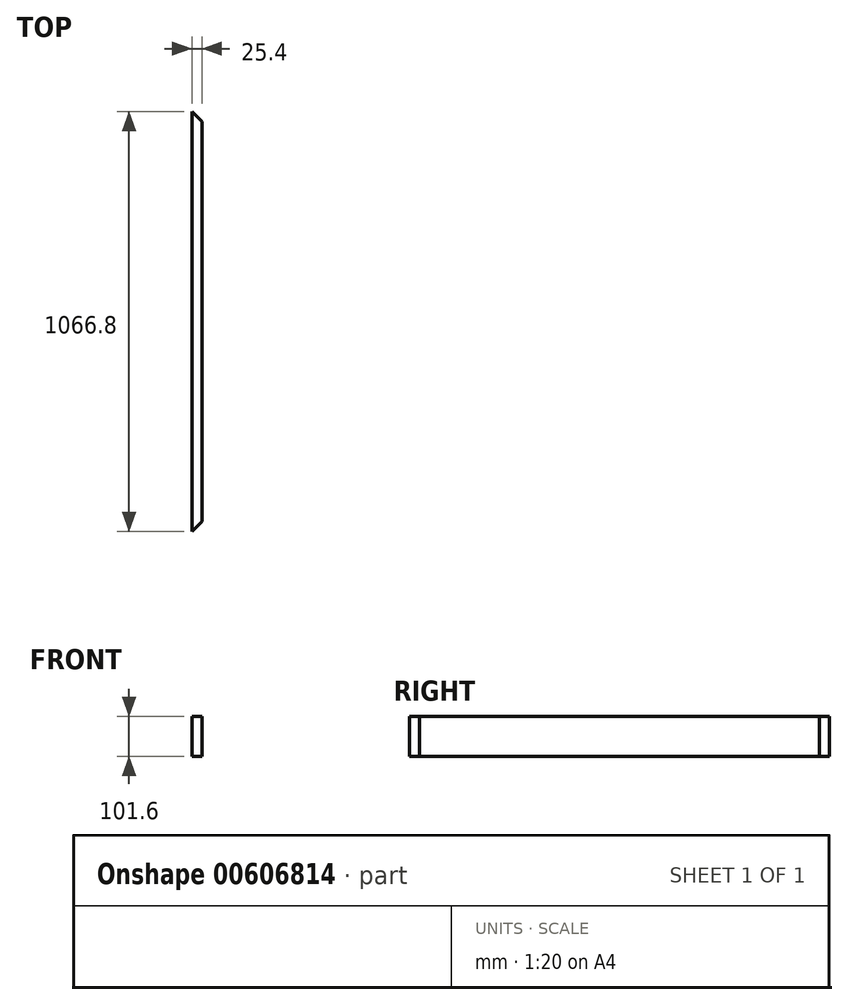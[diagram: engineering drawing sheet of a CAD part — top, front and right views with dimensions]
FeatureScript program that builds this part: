
annotation { "Feature Type Name" : "Feature", "Feature Type Description" : "" }
export const myFeature = defineFeature(function(context is Context, id is Id, definition is map)
    precondition{}
    {
        {
            var Q0;
            Q0=qCreatedBy(makeId("Top.planeOp"),FACE);
            var sketch = newSketch(context, id + "F0", { "sketchPlane" : qUnion([Q0])});
            skLineSegment(sketch, "E0", {"start": v(-11.08, 647.02) * mm, "end": v(14.32, 621.62) * mm});
            skPoint(sketch, "E1.endSnap0", {"position": v(-11.08, 75.52) * mm});
            skLineSegment(sketch, "E2.MirrorCS", {"start": v(-11.08, -546.78) * mm, "end": v(14.32, -521.38) * mm});
            skLineSegment(sketch, "E3", {"start": v(-11.08, -419.78) * mm, "end": v(14.32, -394.38) * mm});
            skLineSegment(sketch, "E4", {"start": v(14.32, 621.62) * mm, "end": v(14.32, -394.38) * mm});
            skLineSegment(sketch, "E5", {"start": v(-11.08, 647.02) * mm, "end": v(-11.08, -419.78) * mm});
            skSolve(sketch);
        }
        {
            var Q0;
            Q0 = qSketchRegion(id + "F0", true);
            extrude(context, id + "F1", {"entities" : qUnion([Q0]), "depth" : 101.6 * mm, "offsetDistance" : 25.4 * mm});
        }
    });
